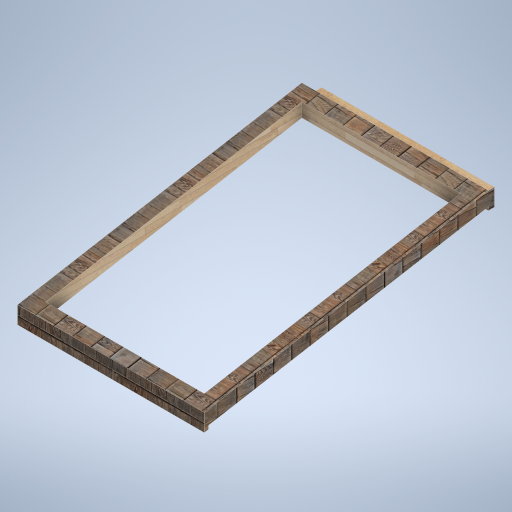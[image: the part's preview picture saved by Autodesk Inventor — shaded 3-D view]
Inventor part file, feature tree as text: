
AUTODESK INVENTOR PART (.ipt)
format: ipt  version: 2024.2 (Build 282272000, 272)  size: 424,448 bytes
history: native  units: mm
features: sketch x8, plane x4, extrude x4, loft x1, other x1, projected_geometry x1
ambient origin geometry x8: Origin, YZ Plane, XZ Plane, XY Plane, X Axis, Y Axis, Z Axis, Center Point
bodies: Body1 (feature_tree)
feature tree (19):
  sketch  "Sketch19"  dims[d29=200.0mm d30=200.0mm]
  plane  "Work Plane17"
  sketch  "Sketch20"  dims[d31=100.0mm d32=150.0mm]
  extrude  "Extrusion4"  Depth=200.0mm
  plane  "Work Plane18"
  sketch  "Sketch22"  dims[d33=2500.0mm d34=51.0mm d35=0.0mm]
  plane  "Work Plane19"
  sketch  "Sketch23"  dims[d36=0.0mm d37=13.962634mm]
  loft  "Loft2"
  extrude  "Extrusion5"  Depth=51.0mm TaperAngle=0.0deg
  plane  "Work Plane20"
  extrude  "Extrusion6"  Depth=13.962634mm
  extrude  "Extrusion7"  TaperAngle=0.0deg  [1 undecoded]
  sketch  "Sketch24"  dims[d38=13.962634mm d39=0.0mm d40=90.0deg]
  other  "Edges1"
  sketch  "Sketch25"  dims[d41=0.0mm d42=90.0deg]
  projected_geometry  "Projected Loop2"
  sketch  "Sketch26"  dims[d43=90.0deg]
  sketch  "Sketch27"  dims[d44=2450.0mm d45=29.670597mm d46=0.0mm d47=0.0mm d48=180.0deg d49=120.0mm d50=120.0mm d51=120.0mm d52=0.0mm d53=0.0mm d54=120.0mm d55=0.0mm d56=0.0mm]
note: 1 required parameter value undecoded (feature->parameter linkage not recoverable at this tier; creation-order binding heuristic only, values carry confidence <= 0.55)
